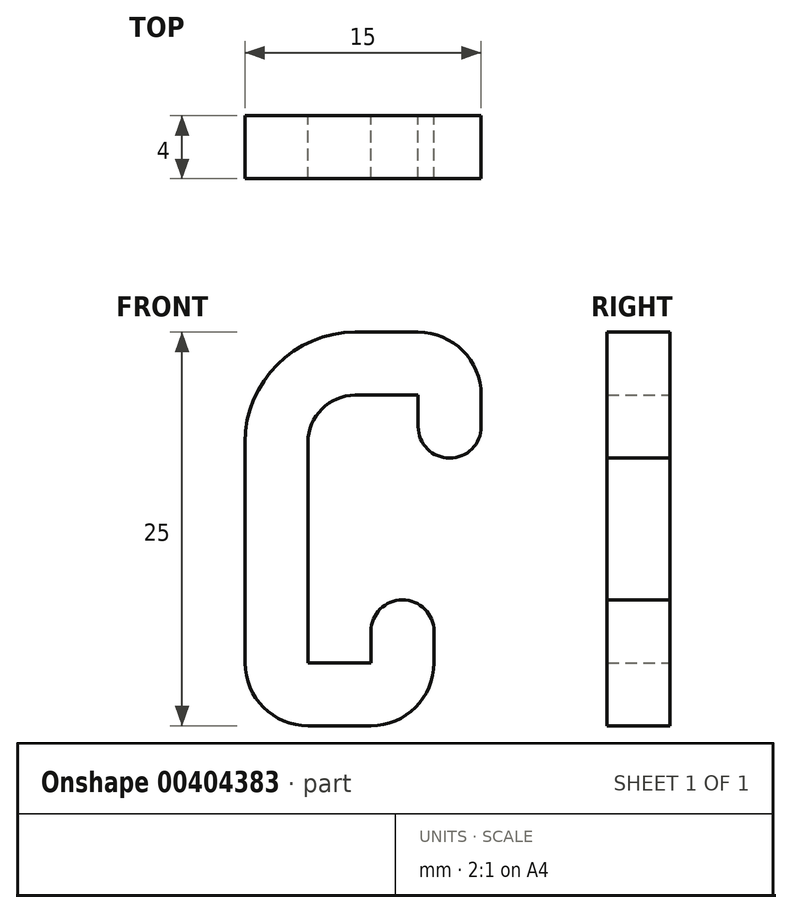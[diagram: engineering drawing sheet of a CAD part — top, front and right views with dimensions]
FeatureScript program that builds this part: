
annotation { "Feature Type Name" : "Feature", "Feature Type Description" : "" }
export const myFeature = defineFeature(function(context is Context, id is Id, definition is map)
    precondition{}
    {
        {
            var Q0;
            Q0=qCreatedBy(makeId("Front.planeOp"),FACE);
            var sketch = newSketch(context, id + "F0", { "sketchPlane" : qUnion([Q0])});
            skLineSegment(sketch, "E0.bottom", {"start": v(9, 12.5) * mm, "end": v(-6, 12.5) * mm});
            skLineSegment(sketch, "E0.top", {"start": v(6, -12.5) * mm, "end": v(-6, -12.5) * mm});
            skLineSegment(sketch, "E0.left", {"start": v(9, 12.5) * mm, "end": v(9, 4.5) * mm});
            skLineSegment(sketch, "E0.right", {"start": v(-6, 12.5) * mm, "end": v(-6, -12.5) * mm});
            skLineSegment(sketch, "E1.bottom", {"start": v(5, 8.5) * mm, "end": v(-2, 8.5) * mm});
            skLineSegment(sketch, "E1.top", {"start": v(2, -8.5) * mm, "end": v(-2, -8.5) * mm});
            skLineSegment(sketch, "E1.left", {"start": v(5, 8.5) * mm, "end": v(5, 4.5) * mm});
            skLineSegment(sketch, "E1.right", {"start": v(-2, 8.5) * mm, "end": v(-2, -8.5) * mm});
            skLineSegment(sketch, "E2.bottom", {"start": v(5, 4.5) * mm, "end": v(9, 4.5) * mm});
            skLineSegment(sketch, "E2.top", {"start": v(2, -4.5) * mm, "end": v(6, -4.5) * mm});
            skLineSegment(sketch, "E3.trimOffspring", {"start": v(2, -4.5) * mm, "end": v(2, -8.5) * mm});
            skLineSegment(sketch, "E4.trimOffspring", {"start": v(6, -4.5) * mm, "end": v(6, -12.5) * mm});
            skSolve(sketch);
        }
        {
            var Q0;
            Q0 = qSketchRegion(id + "F0", true);
            extrude(context, id + "F1", {"entities" : qUnion([Q0]), "depth" : 4 * mm});
        }
        {
            var Q0;
            Q0=makeQuery(id+"F1.opExtrude","SWEPT_EDGE",EDGE,{"disambiguationData":[OSD([sQuery(id+"F0.wireOp",EDGE,"E0.bottom"),sQuery(id+"F0.wireOp",EDGE,"E0.left")])]});
            var Q1;
            Q1=makeQuery(id+"F1.opExtrude","SWEPT_EDGE",EDGE,{"disambiguationData":[OSD([sQuery(id+"F0.wireOp",EDGE,"E0.top"),sQuery(id+"F0.wireOp",EDGE,"E0.right")])]});
            var Q2;
            Q2=makeQuery(id+"F1.opExtrude","SWEPT_EDGE",EDGE,{"disambiguationData":[OSD([sQuery(id+"F0.wireOp",EDGE,"E0.top"),sQuery(id+"F0.wireOp",EDGE,"E4.trimOffspring")])]});
            fillet(context, id + "F2", {"entities" : qUnion([Q0, Q1, Q2]), "radius" : 4 * mm, "tangentPropagation" : true, "allowEdgeOverflow" : false});
        }
        {
            var Q0;
            Q0=makeQuery(id+"F1.opExtrude","SWEPT_EDGE",EDGE,{"disambiguationData":[OSD([sQuery(id+"F0.wireOp",EDGE,"E2.top"),sQuery(id+"F0.wireOp",EDGE,"E4.trimOffspring")])]});
            var Q1;
            Q1=makeQuery(id+"F1.opExtrude","SWEPT_EDGE",EDGE,{"disambiguationData":[OSD([sQuery(id+"F0.wireOp",EDGE,"E2.top"),sQuery(id+"F0.wireOp",EDGE,"E3.trimOffspring")])]});
            var Q2;
            Q2=makeQuery(id+"F1.opExtrude","SWEPT_EDGE",EDGE,{"disambiguationData":[OSD([sQuery(id+"F0.wireOp",EDGE,"E0.left"),sQuery(id+"F0.wireOp",EDGE,"E2.bottom")])]});
            var Q3;
            Q3=makeQuery(id+"F1.opExtrude","SWEPT_EDGE",EDGE,{"disambiguationData":[OSD([sQuery(id+"F0.wireOp",EDGE,"E1.left"),sQuery(id+"F0.wireOp",EDGE,"E2.bottom")])]});
            fillet(context, id + "F3", {"entities" : qUnion([Q0, Q1, Q2, Q3]), "radius" : 2 * mm, "tangentPropagation" : true, "allowEdgeOverflow" : false});
        }
        {
            var Q0;
            Q0=makeQuery(id+"F1.opExtrude","SWEPT_EDGE",EDGE,{"disambiguationData":[OSD([sQuery(id+"F0.wireOp",EDGE,"E1.bottom"),sQuery(id+"F0.wireOp",EDGE,"E1.right")])]});
            fillet(context, id + "F4", {"entities" : qUnion([Q0]), "radius" : 3 * mm, "tangentPropagation" : true, "allowEdgeOverflow" : false});
        }
        {
            var Q0;
            Q0=makeQuery(id+"F1.opExtrude","SWEPT_EDGE",EDGE,{"disambiguationData":[OSD([sQuery(id+"F0.wireOp",EDGE,"E0.bottom"),sQuery(id+"F0.wireOp",EDGE,"E0.right")])]});
            fillet(context, id + "F5", {"entities" : qUnion([Q0]), "radius" : 7 * mm, "tangentPropagation" : true, "allowEdgeOverflow" : false});
        }
    });
